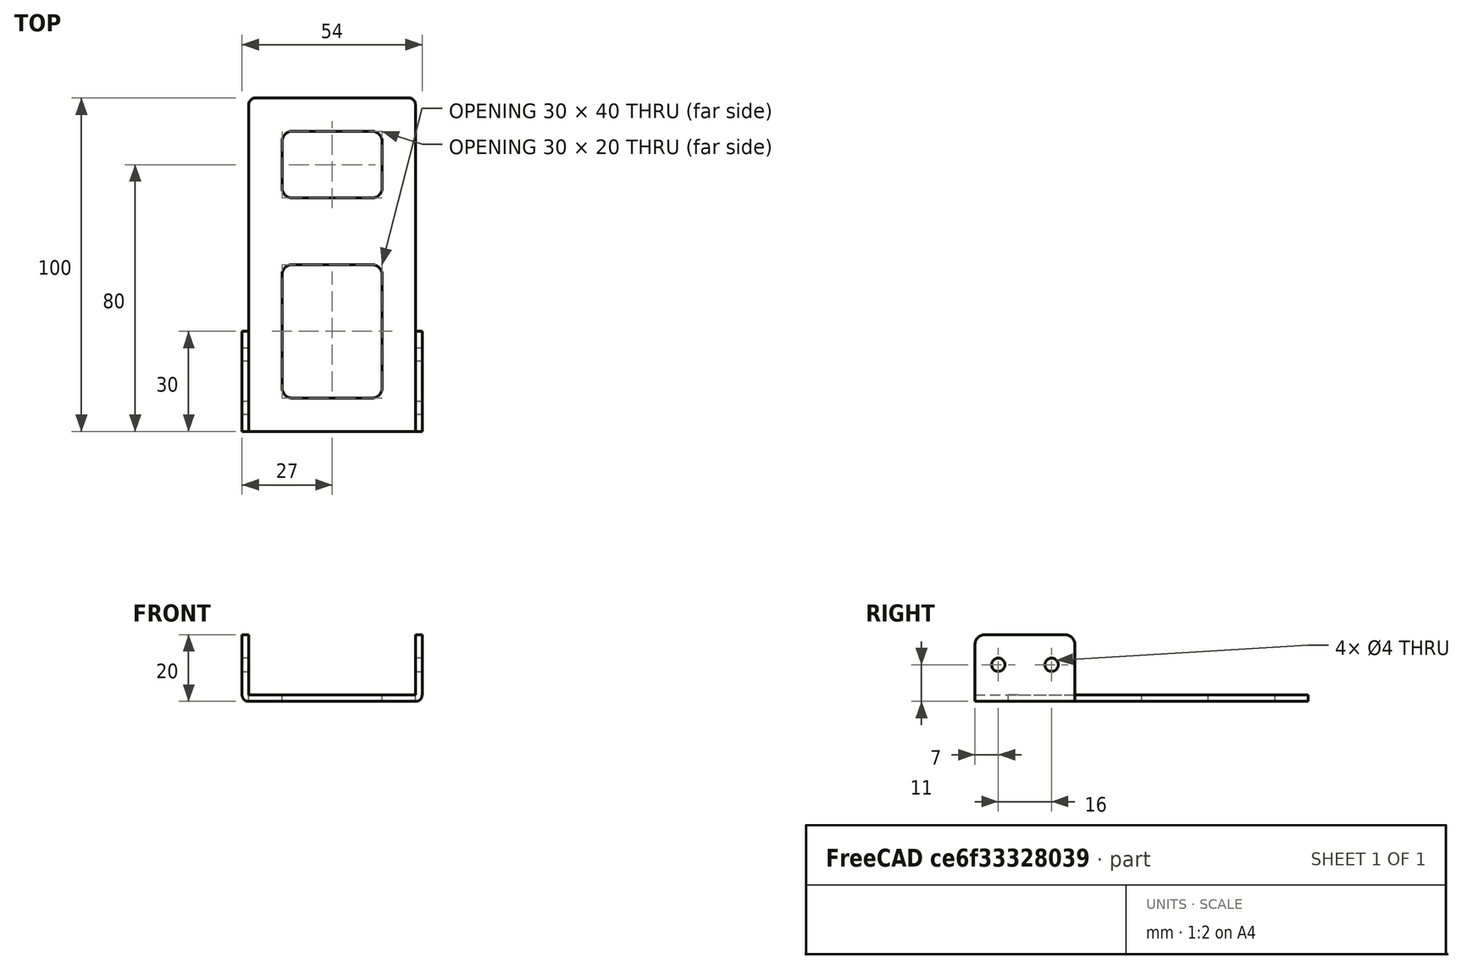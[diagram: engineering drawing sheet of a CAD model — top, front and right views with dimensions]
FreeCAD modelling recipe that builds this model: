
FCSTD DOCUMENT  (FreeCAD 1.0R39319 (Git))
Label: obj_t1_t12_r03Suport
License: All rights reserved
LicenseURL: https://en.wikipedia.org/wiki/All_rights_reserved
objects: Part::Fillet×7, Part::Cut×6, Part::Box×5, Part::Cylinder×4, Part::MultiFuse×2
note: 24 computed .brp shape members not serialized (recipe doc carries the construction recipe); baked Part::Feature solids carry a one-line shape summary decoded from their .brp

FEATURE [Part::Box] Box  label="Cub"
  AttacherType = Attacher::AttachEngine3D
  Height = 2
  Length = 50
  Width = 100
FEATURE [Part::Box] Box001  label="Cub001"
  AttacherType = Attacher::AttachEngine3D
  Height = 10
  Length = 30
  Width = 20
FEATURE [Part::Box] Box002  label="Cub002"
  AttacherType = Attacher::AttachEngine3D
  Height = 10
  Length = 30
  Width = 40
FEATURE [Part::Fillet] Fillet
  Base = -> Box
  EdgeLinks = -> Box [Edge3,Edge7]
  Edges = 2 edges r=2: [Edge3,Edge7]
FEATURE [Part::Fillet] Fillet002  label="forat2"
  Base = -> Box002
  EdgeLinks = -> Box002 [Edge1,Edge3,Edge5,Edge7]
  Edges = 4 edges r=3: [Edge1,Edge3,Edge5,Edge7]
  Placement = pos=(10,10,-5) rot=(0,0,1;0rad)
FEATURE [Part::Fillet] Fillet001  label="forat1"
  Base = -> Box001
  EdgeLinks = -> Box001 [Edge1,Edge3,Edge5,Edge7]
  Edges = 4 edges r=3: [Edge1,Edge3,Edge5,Edge7]
  Placement = pos=(10,70,-5) rot=(0,0,1;0rad)
FEATURE [Part::Cut] Cut
  Base = -> Fillet
  Tool = -> Fillet001
FEATURE [Part::Cut] Cut001  label="base"
  Base = -> Cut
  Placement = pos=(2,0,0) rot=(0,0,1;0rad)
  Tool = -> Fillet002
FEATURE [Part::Box] Box003  label="Cub003"
  AttacherType = Attacher::AttachEngine3D
  Height = 20
  Length = 2
  Width = 30
FEATURE [Part::Cylinder] Cylinder  label="Cilindre"
  Angle = 360
  AttacherType = Attacher::AttachEngine3D
  FirstAngle = 0
  Height = 10
  Placement = pos=(-4,7,11) rot=(0,1,0;1.5708rad)
  Radius = 2
  SecondAngle = 0
FEATURE [Part::Cylinder] Cylinder001  label="Cilindre001"
  Angle = 360
  AttacherType = Attacher::AttachEngine3D
  FirstAngle = 0
  Height = 10
  Placement = pos=(-4,23,11) rot=(0,1,0;1.5708rad)
  Radius = 2
  SecondAngle = 0
FEATURE [Part::Fillet] Fillet003
  Base = -> Box003
  EdgeLinks = -> Box003 [Edge10,Edge12]
  Edges = 2 edges r=3: [Edge10,Edge12]
FEATURE [Part::Cut] Cut002
  Base = -> Fillet003
  Tool = -> Cylinder001
FEATURE [Part::Cut] Cut003  label="suport1"
  Base = -> Cut002
  Tool = -> Cylinder
FEATURE [Part::Box] Box004  label="Cub004"
  AttacherType = Attacher::AttachEngine3D
  Height = 20
  Length = 2
  Width = 30
FEATURE [Part::Cylinder] Cylinder002  label="Cilindre002"
  Angle = 360
  AttacherType = Attacher::AttachEngine3D
  FirstAngle = 0
  Height = 10
  Placement = pos=(-4,7,11) rot=(0,1,0;1.5708rad)
  Radius = 2
  SecondAngle = 0
FEATURE [Part::Cylinder] Cylinder003  label="Cilindre003"
  Angle = 360
  AttacherType = Attacher::AttachEngine3D
  FirstAngle = 0
  Height = 10
  Placement = pos=(-4,23,11) rot=(0,1,0;1.5708rad)
  Radius = 2
  SecondAngle = 0
FEATURE [Part::Fillet] Fillet004
  Base = -> Box004
  EdgeLinks = -> Box004 [Edge10,Edge12]
  Edges = 2 edges r=3: [Edge10,Edge12]
FEATURE [Part::Cut] Cut004
  Base = -> Fillet004
  Tool = -> Cylinder003
FEATURE [Part::Cut] Cut005  label="suport2"
  Base = -> Cut004
  Placement = pos=(52,0,0) rot=(0,0,1;0rad)
  Tool = -> Cylinder002
FEATURE [Part::Fillet] Fillet005
  Base = -> Cut005
  EdgeLinks = -> Cut005 [Edge15]
  Edges = 1 edges r=1.9: [Edge15]
FEATURE [Part::Fillet] Fillet006
  Base = -> Cut003
  EdgeLinks = -> Cut003 [Edge3]
  Edges = 1 edges r=1.9: [Edge3]
FEATURE [Part::MultiFuse] Fusion
  Shapes = -> [Fillet006,Fillet005]
FEATURE [Part::MultiFuse] Fusion001
  Shapes = -> [Fillet006,Fillet005,Fusion,Cut001]
